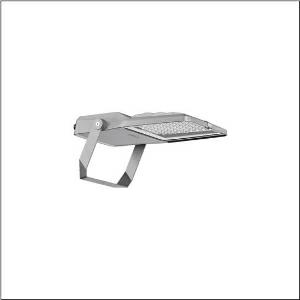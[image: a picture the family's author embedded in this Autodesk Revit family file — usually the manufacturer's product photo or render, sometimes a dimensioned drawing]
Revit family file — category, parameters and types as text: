
# Revit family: floodlight_fl_21_mini___pl52_5xa7773c2d1a_dd61
name_source: partatom
category: Lighting Fixtures
units: mm (PartAtom-declared; Revit-internal decimal feet)

## family parameters
Cut with Voids When Loaded = No
Host = Face
Light Source = No
Part Type = Normal
Room Calculation Point = No
Round Connector Dimension = Use Diameter
Shared = No

## types (1)
- --- (1 x LED, 19510 lm, 163.5 W, 3000K)
    Apparent Load = 163 VA
    CIE Flux Codes = 26 60 98 100 100
    Color Rendering = 70
    Color Temperature = 3000K
    Default Elevation = 1800 mm
    Description = Floodlight FL 21 mini, floodlight, primary light control with lens, of PMMA, primary optical cover: protective disc, of toughened safety glass, transparent, light distribution: PL52, light emission: direct distribution, installation type: surface-mounted, LED, High Power LED, rated luminous flux: 19.510lm, luminous efficacy: 119lm/W, light colour: 730, colour temperature: 3000K, control gear: ON/OFF Multilumen, control: Temp-Guard, with terminal, 6-pole, mains connection: 220..240V, AC, 50/60Hz, start of lifetime: 164W, luminaire housing, of diecast aluminium, powder-coated, Siteco® metallic grey (DB 702S), corrosivity category C5 mid according to DIN EN ISO 12944, suitable for swimming pools, chlorine-resistant, sealing non-destructively replaceable, mounting bracket, of steel, galvanised, powder-coated, Siteco® metallic grey (DB 702S), ON/OFF, protection rating (complete): IP66, insulation class (complete): insulation class I (protective earthing), certification: CE, ENEC, VDE, protection symbol: D, impact resistance: IK08, permissible operating ambient temperature: -40..+40°C, permissible operating ambient temperature for outdoor applications: -40..+50°C, standard: DIN EN 12944, LABS conformity tested according to VDMA 24364:2018-05, packaging unit: 1 piece

Light Distribution: PL52
    Height = 70 mm
    Lamp = 1 x LED
    Lamp Light Flux = 19510 lm
    Lamp Power = 163.5 W
    Lamp count = 1
    Length = 485 mm
    Luminous efficacy = 119 lm/W
    Manufacturer = Siteco
    ModVariant = No
    Model = 5XA7773C2D1A
    Number of Poles = 1
    OnlyDefault = Yes
    Power Factor = 1
    Product Name = Floodlight FL 21 mini | PL52
    Product group = floodlight | pylon annexe
    ProductGroupID = 6201
    Protection Class = Protection class I
    Protection Degree = IP 66
    RLX_Detail_Level = 1
    RLX_Emergency_Light_Flux = 0 lm
    RLX_Emergency_Type = 0
    RLX_Emergency_Type_DB = No
    RlxData = <blob elided: 94429 chars, md5=6c711f4c>
    Socket = socket
    Standby Power = 0 W
    System Light Flux = 19510 lm
    System Power = 163 W
    Type Comments = factory setting: luminous flux: 100 % | (ON | - | - | - | - | - | - | -) | 825 mA
    Type Image = l_1006845.jpg
    URL = http://relux.com
    VarID = @adj_185565
    Voltage = 0 V
    Weight = 0.00 kg
    Width = 337 mm

## geometry (parser evidence)
native form markers: Blend x4, Sweep x11
no freeform markers — native parametric forms only
